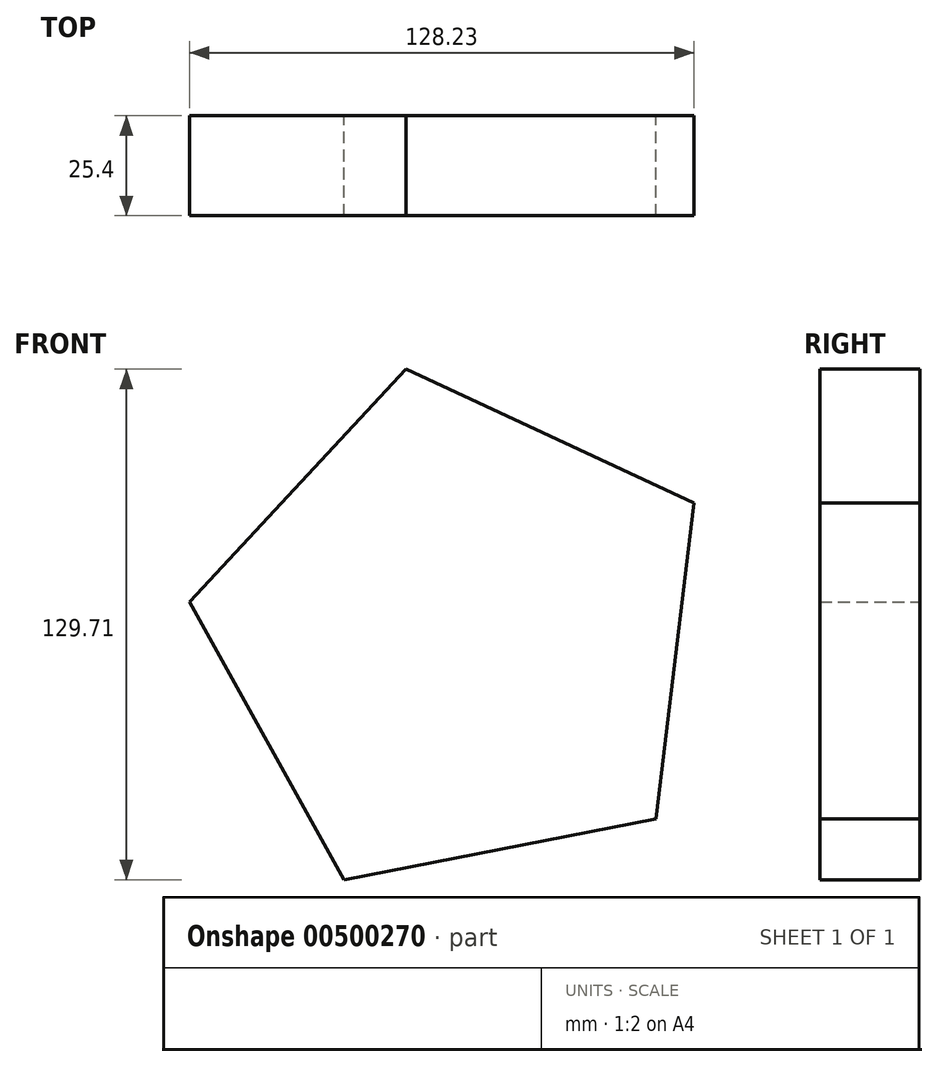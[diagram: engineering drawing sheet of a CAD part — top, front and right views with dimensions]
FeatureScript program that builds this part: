
annotation { "Feature Type Name" : "Feature", "Feature Type Description" : "" }
export const myFeature = defineFeature(function(context is Context, id is Id, definition is map)
    precondition{}
    {
        {
            var Q0;
            Q0=qCreatedBy(makeId("Front.planeOp"),FACE);
            var sketch = newSketch(context, id + "F0", { "sketchPlane" : qUnion([Q0])});
            skCircle(sketch, "E0.cCircle", {"center": v(0, 0) * mm, "radius": 68.7 * mm, "construction": true});
            skLineSegment(sketch, "E0.0", {"start": v(60.04, 33.37) * mm, "end": v(50.3, -46.8) * mm});
            skLineSegment(sketch, "E0.1", {"start": v(50.3, -46.8) * mm, "end": v(-28.96, -62.3) * mm});
            skLineSegment(sketch, "E0.2", {"start": v(-28.96, -62.3) * mm, "end": v(-68.2, 8.3) * mm});
            skLineSegment(sketch, "E0.3", {"start": v(-68.2, 8.3) * mm, "end": v(-13.19, 67.42) * mm});
            skLineSegment(sketch, "E0.4", {"start": v(-13.19, 67.42) * mm, "end": v(60.04, 33.37) * mm});
            skSolve(sketch);
        }
        {
            var Q0;
            Q0=makeQuery(id+"F0.imprint","IMPRINT",FACE,{"disambiguationData":[TD([[makeQuery(id+"F0.imprint","IMPRINT",EDGE,{"derivedFrom":sQuery(id+"F0.wireOp",EDGE,"E0.0")}),-1.0]])]});
            extrude(context, id + "F1", {"entities" : qUnion([Q0]), "depth" : 25.4 * mm});
        }
    });
